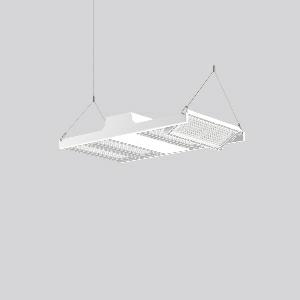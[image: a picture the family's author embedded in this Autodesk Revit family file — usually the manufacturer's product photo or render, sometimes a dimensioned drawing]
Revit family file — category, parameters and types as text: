
# Revit family: light_case_921688_002_1_76_e064
name_source: partatom
category: Lighting Fixtures
units: mm (PartAtom-declared; Revit-internal decimal feet)

## family parameters
Cut with Voids When Loaded = No
Host = Face
Light Source = No
Part Type = Normal
Room Calculation Point = No
Round Connector Dimension = Use Diameter
Shared = No

## types (1)
- LIGHT CASE (1 x LED Modul 865, 8700 lm, 6500)
    Apparent Load = 225 VA
    CIE Flux Codes = 80 98 100 100 100
    Color Rendering = 80
    Color Temperature = 6500
    Default Elevation = 1800 mm
    Description = Series: LIGHT CASE
Flat highbay luminaire for chain or cable suspension with 4 LED modules that can be swivelled. Housing: die cast aluminium and sheet steel, powder-coated. Optimised thermal management thanks to special luminaire design. Self-cleaning heat sink for constant heat dissipation. Cover: plastic (polycarbonate, shockproof), with integrated four-row lens system. LED modules can be swivelled ± 30° for optimum illumination. Suitable for chain or steel cable suspension (to be provided on site). With 5-pin connection terminal (1.5 m). With integrated movement sensor and light sensor for daylight detection on request. Ball impact proof in accordance with DIN 18032-03 (except steel cable suspension). Luminaire with limited surface temperature in accordance with EN 60598-2-24 for use in environments in which a deposit of conductive dust on the luminaire can be expected. 
Colour: white
Length: 680 mm
Width: 397 mm
Height: 110 mm
Lamp: LED
Socket: without socket
Colour temperature: 6500K
Colour rendering index (CRI): 80
System power: 225 W
Rated luminous flux: 34800 lm
Luminous efficiency: 155 lm/W
Control gear: Converter, dimmable, DALI
Protection class: I
Type of protection: IP 65
    Height = 110 mm
    Lamp = 1 x LED Modul 865
    Lamp Light Flux = 8700 lm
    Lamp count = 1
    Length = 680 mm
    Lifetime = 50000 h
    Luminous efficacy = 155 lm/W
    Manufacturer = RZB
    ModVariant = No
    Model = 921688.002.1.76
    Mounting Place = Ceiling
    Mounting Type = Pendant
    Number of Poles = 1
    OnlyDefault = Yes
    Power Factor = 1
    Product Name = LIGHT CASE
    Product group = Pendant commercial luminaires
    ProductGroupID = 903
    Protection Class = Protection class I
    Protection Degree = IP 65
    RLX_Detail_Level = 1
    RLX_Emergency_Light_Flux = 0 lm
    RLX_Emergency_Type = 0
    RLX_Emergency_Type_DB = No
    RlxData = <blob elided: 26873 chars, md5=7d47f02c>
    Socket = socket
    Standby Power = 0 W
    System Light Flux = 34800 lm
    System Power = 225 W
    Type Comments = Product without accessories
    Type Image = 921523.002.76.jpg
    URL = http://relux.com
    VarID = ---
    Voltage = 230 V
    Voltage Range = 220-240 V
    Weight = 0.00 kg
    Width = 397 mm

## geometry (parser evidence)
native form markers: Blend x4, Sweep x22
no freeform markers — native parametric forms only
